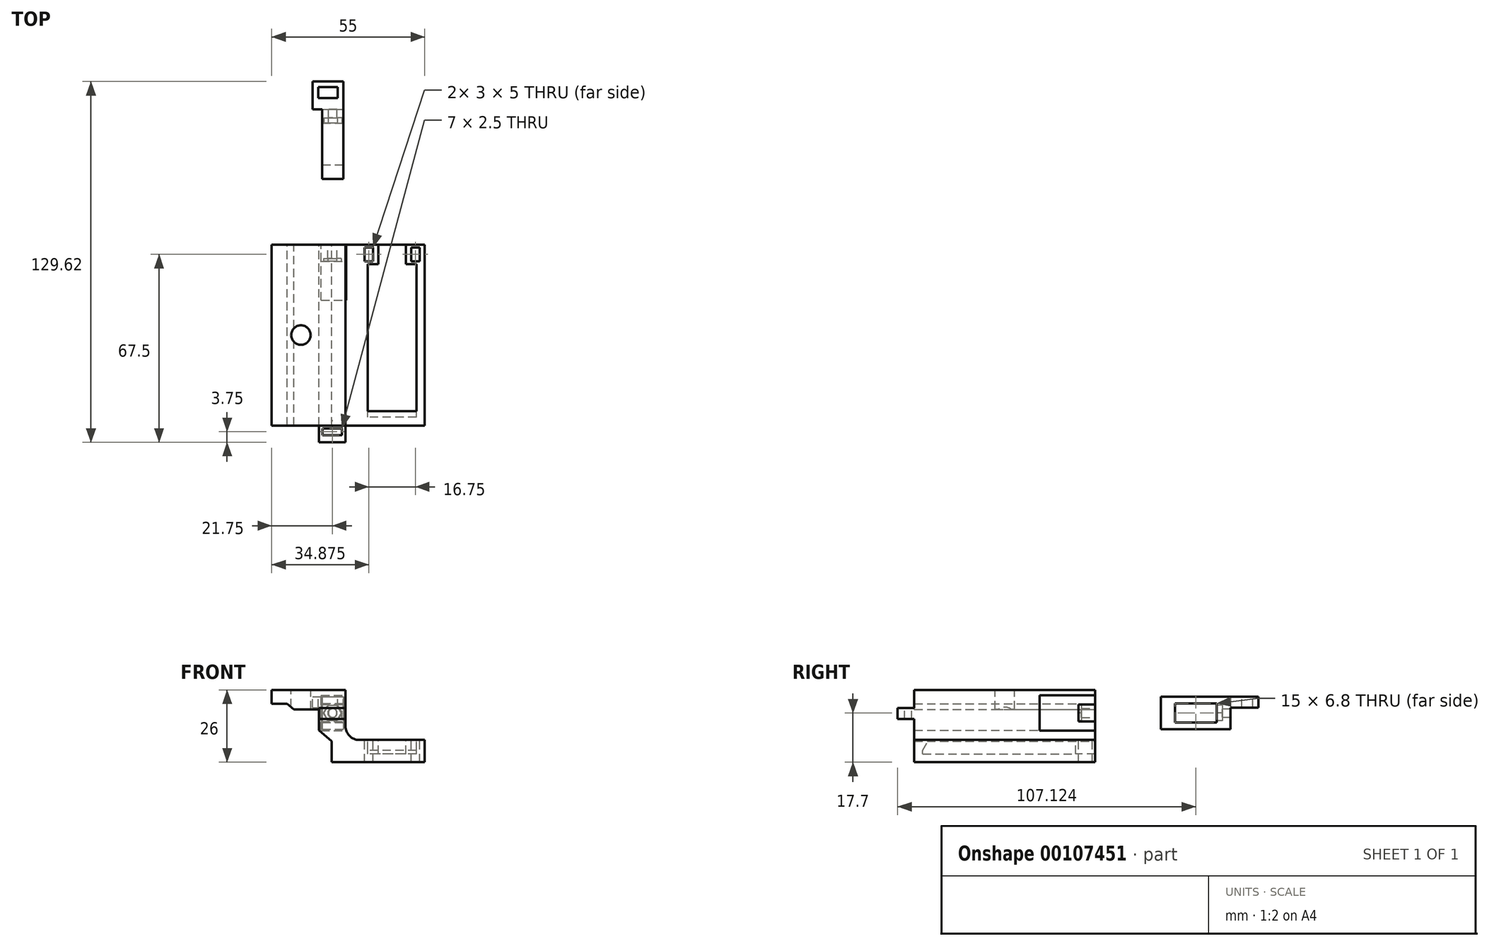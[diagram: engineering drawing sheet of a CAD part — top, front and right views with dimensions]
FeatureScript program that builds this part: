
annotation { "Feature Type Name" : "Feature", "Feature Type Description" : "" }
export const myFeature = defineFeature(function(context is Context, id is Id, definition is map)
    precondition{}
    {
        {
            var Q0;
            Q0=qCreatedBy(makeId("Front.planeOp"),FACE);
            var sketch = newSketch(context, id + "F0", { "sketchPlane" : qUnion([Q0])});
            skLineSegment(sketch, "E0", {"start": v(0, 0) * mm, "end": v(0, 21) * mm, "construction": true});
            skLineSegment(sketch, "E1", {"start": v(0, 0) * mm, "end": v(21.5, 0) * mm, "construction": true});
            skLineSegment(sketch, "E2", {"start": v(0, 21) * mm, "end": v(5.5, 21) * mm});
            skLineSegment(sketch, "E3", {"start": v(8, 19) * mm, "end": v(17, 19) * mm});
            skLineSegment(sketch, "E4", {"start": v(17, 19) * mm, "end": v(17, 11.5) * mm});
            skLineSegment(sketch, "E5", {"start": v(21.5, 0) * mm, "end": v(21.5, 7.5) * mm});
            skLineSegment(sketch, "E6", {"start": v(17, 11.5) * mm, "end": v(21.5, 7.5) * mm});
            skLineSegment(sketch, "E7", {"start": v(5.5, 21) * mm, "end": v(8, 19) * mm});
            skLineSegment(sketch, "E8", {"start": v(0, 21) * mm, "end": v(0, 26) * mm});
            skLineSegment(sketch, "E9", {"start": v(26.5, 13) * mm, "end": v(26.5, 26) * mm});
            skLineSegment(sketch, "E10", {"start": v(0, 26) * mm, "end": v(26.5, 26) * mm});
            skLineSegment(sketch, "E11", {"start": v(21.5, 0) * mm, "end": v(55, 0) * mm});
            skLineSegment(sketch, "E12", {"start": v(55, 0) * mm, "end": v(55, 8) * mm});
            skLineSegment(sketch, "E13", {"start": v(55, 8) * mm, "end": v(31.5, 8) * mm});
            skPoint(sketch, "E14.visualSharp", {"position": v(26.5, 26) * mm});
            skPoint(sketch, "E15.visualSharp", {"position": v(26.5, 8) * mm});
            skArc(sketch, "E15.filletArc", {"start": v(26.5, 13) * mm, "mid": v(27.96, 9.46) * mm, "end": v(31.5, 8) * mm});
            skSolve(sketch);
        }
        {
            var Q0;
            Q0=makeQuery(id+"F0.imprint","IMPRINT",FACE,{"disambiguationData":[TD([[makeQuery(id+"F0.imprint","IMPRINT",EDGE,{"derivedFrom":sQuery(id+"F0.wireOp",EDGE,"E2")}),1.0]])]});
            extrude(context, id + "F1", {"entities" : qUnion([Q0]), "depth" : 65 * mm});
        }
        {
            var Q0;
            Q0=makeQuery(id+"F1.opExtrude","SWEPT_FACE",FACE,{"disambiguationData":[OSD([sQuery(id+"F0.wireOp",EDGE,"E10")])]});
            var sketch = newSketch(context, id + "F2", { "sketchPlane" : qUnion([Q0])});
            skLineSegment(sketch, "E16", {"start": v(10.5, 0) * mm, "end": v(10.5, -65) * mm, "construction": true});
            skCircle(sketch, "E17", {"center": v(10.5, -32.5) * mm, "radius": 3.5 * mm});
            skSolve(sketch);
        }
        {
            var Q0;
            Q0=makeQuery(id+"F2.imprint","IMPRINT",FACE,{"disambiguationData":[TD([[makeQuery(id+"F2.imprint","IMPRINT",EDGE,{"derivedFrom":sQuery(id+"F2.wireOp",EDGE,"E17")}),1.0]])]});
            extrude(context, id + "F3", {"entities" : qUnion([Q0]), "operationType" : NewBodyOperationType.REMOVE, "endBound" : BoundingType.UP_TO_NEXT, "oppositeDirection" : true, "depth" : 25 * mm});
        }
        {
            var Q0;
            Q0=makeQuery(id+"F1.opExtrude","SWEPT_FACE",FACE,{"disambiguationData":[OSD([sQuery(id+"F0.wireOp",EDGE,"E13")])]});
            var sketch = newSketch(context, id + "F4", { "sketchPlane" : qUnion([Q0])});
            skLineSegment(sketch, "E18.bottom", {"start": v(52, -62) * mm, "end": v(34.5, -62) * mm});
            skLineSegment(sketch, "E18.top", {"start": v(52, -7) * mm, "end": v(48.25, -7) * mm});
            skLineSegment(sketch, "E18.left", {"start": v(52, -62) * mm, "end": v(52, -7) * mm});
            skLineSegment(sketch, "E18.right", {"start": v(34.5, -62) * mm, "end": v(34.5, -7) * mm});
            skLineSegment(sketch, "E19", {"start": v(38.25, -7) * mm, "end": v(38.25, 0) * mm});
            skLineSegment(sketch, "E20", {"start": v(38.25, 0) * mm, "end": v(48.25, 0) * mm});
            skLineSegment(sketch, "E21", {"start": v(48.25, 0) * mm, "end": v(48.25, -7) * mm});
            skLineSegment(sketch, "E22.trimOffspring", {"start": v(38.25, -7) * mm, "end": v(34.5, -7) * mm});
            skLineSegment(sketch, "E23", {"start": v(43.25, -62) * mm, "end": v(43.25, -65) * mm, "construction": true});
            skSolve(sketch);
        }
        {
            var Q0;
            Q0=makeQuery(id+"F4.imprint","IMPRINT",FACE,{"disambiguationData":[TD([[makeQuery(id+"F4.imprint","IMPRINT",EDGE,{"derivedFrom":sQuery(id+"F4.wireOp",EDGE,"E18.bottom")}),-1.0]])]});
            extrude(context, id + "F5", {"entities" : qUnion([Q0]), "operationType" : NewBodyOperationType.REMOVE, "oppositeDirection" : true, "depth" : 5 * mm});
        }
        {
            var Q0;
            Q0=makeQuery(id+"F5.boolean.opBoolean","COPY",FACE,{"derivedFrom":makeQuery(id+"F5.opExtrude","SWEPT_FACE",FACE,{"disambiguationData":[OSD([sQuery(id+"F4.wireOp",EDGE,"E18.right")])]})});
            var sketch = newSketch(context, id + "F6", { "sketchPlane" : qUnion([Q0])});
            skLineSegment(sketch, "E24", {"start": v(-62, 4.3) * mm, "end": v(-59.86, 8) * mm});
            skSolve(sketch);
        }
        {
            var Q0;
            {var subQ0=sQuery(id+"F6.wireOp",EDGE,"E24");Q0=makeQuery(id+"F6.imprint","IMPRINT",FACE,{"disambiguationData":[TD([[makeQuery(id+"F6.imprint","IMPRINT",EDGE,{"derivedFrom":subQ0}),1.0]])]});}
            extrude(context, id + "F7", {"entities" : qUnion([Q0]), "operationType" : NewBodyOperationType.ADD, "endBound" : BoundingType.UP_TO_NEXT, "depth" : 25 * mm});
        }
        {
            var Q0;
            Q0=makeQuery(id+"F1.opExtrude","SWEPT_FACE",FACE,{"disambiguationData":[OSD([sQuery(id+"F0.wireOp",EDGE,"E9")])]});
            cPlane(context, id + "F8", {"entities" : qUnion([Q0]), "cplaneType" : CPlaneType.OFFSET, "offset" : 0 * mm, "oppositeDirection" : true, "width" : 150 * mm, "height" : 150 * mm});
        }
        {
            var Q0;
            Q0=qCreatedBy(id+"F8.planeOp",FACE);
            var sketch = newSketch(context, id + "F9", { "sketchPlane" : qUnion([Q0])});
            skLineSegment(sketch, "E25.bottom", {"start": v(-58, 13) * mm, "end": v(0, 13) * mm});
            skLineSegment(sketch, "E25.top", {"start": v(-65, 15.5) * mm, "end": v(0, 15.5) * mm});
            skLineSegment(sketch, "E25.right", {"start": v(0, 13) * mm, "end": v(0, 15.5) * mm});
            skLineSegment(sketch, "E26.left", {"start": v(-65, 15.5) * mm, "end": v(-65, 13) * mm});
            skPoint(sketch, "E27", {"position": v(-29, 13) * mm});
            skLineSegment(sketch, "E28", {"start": v(-29, 18.78) * mm, "end": v(-29, 7.34) * mm, "construction": true});
            skLineSegment(sketch, "E29.MirrorCS", {"start": v(0, 15.5) * mm, "end": v(0, 13) * mm});
            skLineSegment(sketch, "E30.MirrorCS", {"start": v(7, 15.5) * mm, "end": v(7, 13) * mm});
            skLineSegment(sketch, "E31.bottom", {"start": v(-65, 15.5) * mm, "end": v(-71, 15.5) * mm});
            skLineSegment(sketch, "E31.top", {"start": v(-65, 19.5) * mm, "end": v(-71, 19.5) * mm});
            skLineSegment(sketch, "E31.left", {"start": v(-65, 15.5) * mm, "end": v(-65, 19.5) * mm});
            skLineSegment(sketch, "E31.right", {"start": v(-71, 15.5) * mm, "end": v(-71, 19.5) * mm});
            skLineSegment(sketch, "E32.MirrorCS", {"start": v(7, 15.5) * mm, "end": v(7, 19.5) * mm});
            skSolve(sketch);
        }
        {
            var Q0;
            Q0=makeQuery(id+"F9.imprint","IMPRINT",FACE,{"disambiguationData":[TD([[makeQuery(id+"F9.imprint","IMPRINT",EDGE,{"derivedFrom":sQuery(id+"F9.wireOp",EDGE,"E31.bottom")}),-1.0]])]});
            var Q1;
            Q1=makeQuery(id+"F9.imprint","IMPRINT",FACE,{"disambiguationData":[TD([[makeQuery(id+"F9.imprint","IMPRINT",EDGE,{"derivedFrom":sQuery(id+"F9.wireOp",EDGE,"28a8ac16-13eb-431f-9eda-ab6bdd291a540.MirrorCS")}),-1.0]])]});
            var Q2;
            Q2=makeQuery(id+"F1.opExtrude","SWEPT_FACE",FACE,{"disambiguationData":[OSD([sQuery(id+"F0.wireOp",EDGE,"E4")])]});
            extrude(context, id + "F10", {"entities" : qUnion([Q0, Q1]), "operationType" : NewBodyOperationType.ADD, "endBound" : BoundingType.UP_TO_SURFACE, "oppositeDirection" : true, "endBoundEntityFace" : qUnion([Q2]), "depth" : 25 * mm});
        }
        {
            var Q0;
            Q0=makeQuery(id+"F10.opExtrude","SWEPT_FACE",FACE,{"disambiguationData":[OSD([sQuery(id+"F9.wireOp",EDGE,"E31.top")])]});
            var sketch = newSketch(context, id + "F11", { "sketchPlane" : qUnion([Q0])});
            skLineSegment(sketch, "E33.bottom", {"start": v(18.25, -66) * mm, "end": v(25.25, -66) * mm});
            skLineSegment(sketch, "E33.top", {"start": v(18.25, -68.5) * mm, "end": v(25.25, -68.5) * mm});
            skLineSegment(sketch, "E33.left", {"start": v(18.25, -66) * mm, "end": v(18.25, -68.5) * mm});
            skLineSegment(sketch, "E33.right", {"start": v(25.25, -66) * mm, "end": v(25.25, -68.5) * mm});
            skLineSegment(sketch, "E34", {"start": v(21.75, -71) * mm, "end": v(21.75, -68.5) * mm, "construction": true});
            skSolve(sketch);
        }
        {
            var Q0;
            Q0=makeQuery(id+"F11.imprint","IMPRINT",FACE,{"disambiguationData":[TD([[makeQuery(id+"F11.imprint","IMPRINT",EDGE,{"derivedFrom":sQuery(id+"F11.wireOp",EDGE,"E33.bottom")}),-1.0]])]});
            extrude(context, id + "F12", {"entities" : qUnion([Q0]), "operationType" : NewBodyOperationType.REMOVE, "endBound" : BoundingType.UP_TO_NEXT, "oppositeDirection" : true, "depth" : 25 * mm});
        }
        {
            var Q0;
            Q0=qCreatedBy(id+"F8.planeOp",FACE);
            cPlane(context, id + "F13", {"entities" : qUnion([Q0]), "cplaneType" : CPlaneType.OFFSET, "offset" : 0.75 * mm, "oppositeDirection" : true, "width" : 150 * mm, "height" : 150 * mm});
        }
        {
            var Q0;
            Q0=qCreatedBy(id+"F13.planeOp",FACE);
            var sketch = newSketch(context, id + "F14", { "sketchPlane" : qUnion([Q0])});
            skLineSegment(sketch, "E35", {"start": v(0, 11.4) * mm, "end": v(-20, 11.4) * mm});
            skLineSegment(sketch, "E36", {"start": v(-20, 24) * mm, "end": v(0, 24) * mm});
            skLineSegment(sketch, "E37", {"start": v(0, 24) * mm, "end": v(0, 20.7) * mm});
            skLineSegment(sketch, "E38", {"start": v(0, 20.7) * mm, "end": v(-6, 20.7) * mm});
            skLineSegment(sketch, "E39", {"start": v(-6, 20.7) * mm, "end": v(-6, 14.7) * mm});
            skLineSegment(sketch, "E40", {"start": v(-6, 14.7) * mm, "end": v(0, 14.7) * mm});
            skLineSegment(sketch, "E41", {"start": v(0, 14.7) * mm, "end": v(0, 11.4) * mm});
            skLineSegment(sketch, "E42", {"start": v(-20, 11.4) * mm, "end": v(-20, 24) * mm});
            skSolve(sketch);
        }
        {
            var Q0;
            Q0=makeQuery(id+"F14.imprint","IMPRINT",FACE,{"disambiguationData":[TD([[makeQuery(id+"F14.imprint","IMPRINT",EDGE,{"derivedFrom":sQuery(id+"F14.wireOp",EDGE,"E35")}),-1.0]])]});
            extrude(context, id + "F15", {"entities" : qUnion([Q0]), "operationType" : NewBodyOperationType.REMOVE, "oppositeDirection" : true, "depth" : 8 * mm});
        }
        {
            var Q0;
            Q0=makeQuery(id+"F1.opExtrude","CAP_FACE",FACE,{"disambiguationData":[OSD([sQuery(id+"F0.wireOp",EDGE,"E2"),sQuery(id+"F0.wireOp",EDGE,"E3"),sQuery(id+"F0.wireOp",EDGE,"E4"),sQuery(id+"F0.wireOp",EDGE,"E5"),sQuery(id+"F0.wireOp",EDGE,"E6"),sQuery(id+"F0.wireOp",EDGE,"E7"),sQuery(id+"F0.wireOp",EDGE,"E8"),sQuery(id+"F0.wireOp",EDGE,"E9"),sQuery(id+"F0.wireOp",EDGE,"E10"),sQuery(id+"F0.wireOp",EDGE,"E11"),sQuery(id+"F0.wireOp",EDGE,"E12"),sQuery(id+"F0.wireOp",EDGE,"E13"),sQuery(id+"F0.wireOp",EDGE,"E14.filletArc"),sQuery(id+"F0.wireOp",EDGE,"E15.filletArc")])],"isStart":true});
            var sketch = newSketch(context, id + "F16", { "sketchPlane" : qUnion([Q0])});
            skLineSegment(sketch, "E43", {"start": v(-25.75, 17.7) * mm, "end": v(-17.75, 17.7) * mm, "construction": true});
            skPoint(sketch, "E44", {"position": v(-21.75, 17.7) * mm});
            skCircle(sketch, "E45", {"center": v(-21.75, 17.7) * mm, "radius": 1.65 * mm});
            skPoint(sketch, "E46.0.midPoint", {"position": v(-21.05, 15.93) * mm});
            skLineSegment(sketch, "E47", {"start": v(-17.75, 20.7) * mm, "end": v(-17.75, 14.7) * mm, "construction": true});
            skSolve(sketch);
        }
        {
            var Q0;
            Q0=makeQuery(id+"F16.imprint","IMPRINT",FACE,{"disambiguationData":[TD([[makeQuery(id+"F16.imprint","IMPRINT",EDGE,{"derivedFrom":sQuery(id+"F16.wireOp",EDGE,"E45")}),1.0]])]});
            extrude(context, id + "F17", {"entities" : qUnion([Q0]), "operationType" : NewBodyOperationType.REMOVE, "endBound" : BoundingType.UP_TO_NEXT, "oppositeDirection" : true, "depth" : 25 * mm});
        }
        {
            var Q0;
            Q0=makeQuery(id+"F15.boolean.opBoolean","COPY",FACE,{"derivedFrom":makeQuery(id+"F15.opExtrude","SWEPT_FACE",FACE,{"disambiguationData":[OSD([sQuery(id+"F14.wireOp",EDGE,"E39")])]})});
            var sketch = newSketch(context, id + "F18", { "sketchPlane" : qUnion([Q0])});
            skCircle(sketch, "E48.cCircle", {"center": v(21.75, 17.7) * mm, "radius": 2.75 * mm, "construction": true});
            skLineSegment(sketch, "E48.0", {"start": v(24.93, 17.7) * mm, "end": v(23.34, 14.95) * mm});
            skLineSegment(sketch, "E48.1", {"start": v(23.34, 14.95) * mm, "end": v(20.16, 14.95) * mm});
            skLineSegment(sketch, "E48.2", {"start": v(20.16, 14.95) * mm, "end": v(18.57, 17.7) * mm});
            skLineSegment(sketch, "E48.3", {"start": v(18.57, 17.7) * mm, "end": v(20.16, 20.45) * mm});
            skLineSegment(sketch, "E48.4", {"start": v(20.16, 20.45) * mm, "end": v(23.34, 20.45) * mm});
            skLineSegment(sketch, "E48.5", {"start": v(23.34, 20.45) * mm, "end": v(24.93, 17.7) * mm});
            skPoint(sketch, "E48.0.midPoint", {"position": v(24.13, 16.33) * mm});
            skSolve(sketch);
        }
        {
            var Q0;
            {var subQ1=sQuery(id+"F18.wireOp",EDGE,"E48.1");Q0=makeQuery(id+"F18.imprint","IMPRINT",FACE,{"disambiguationData":[TD([[makeQuery(id+"F18.imprint","IMPRINT",EDGE,{"derivedFrom":subQ1}),-1.0]])]});}
            extrude(context, id + "F19", {"entities" : qUnion([Q0]), "operationType" : NewBodyOperationType.REMOVE, "oppositeDirection" : true, "depth" : 1 * mm});
        }
        {
            var Q0;
            Q0 = qSketchRegion(id + "F14", true);
            extrude(context, id + "F20", {"entities" : qUnion([Q0]), "operationType" : NewBodyOperationType.REMOVE, "endBound" : BoundingType.UP_TO_NEXT, "oppositeDirection" : true, "depth" : 25 * mm});
        }
        {
            var Q0;
            Q0 = qSketchRegion(id + "F14", true);
            extrude(context, id + "F21", {"entities" : qUnion([Q0]), "operationType" : NewBodyOperationType.REMOVE, "endBound" : BoundingType.UP_TO_NEXT, "depth" : 25 * mm});
        }
        {
            var Q0;
            Q0=makeQuery(id+"F7.boolean.opBoolean","MERGE",FACE,{"derivedFrom":[makeQuery(id+"F1.opExtrude","SWEPT_FACE",FACE,{"disambiguationData":[OSD([sQuery(id+"F0.wireOp",EDGE,"E13")])]}),makeQuery(id+"F7.opExtrude","SWEPT_FACE",FACE,{"disambiguationData":[OSD([sQuery(id+"F4.wireOp",EDGE,"E18.right")])]})]});
            var sketch = newSketch(context, id + "F22", { "sketchPlane" : qUnion([Q0])});
            skLineSegment(sketch, "E49.bottom", {"start": v(36.38, -1) * mm, "end": v(33.38, -1) * mm});
            skLineSegment(sketch, "E49.top", {"start": v(36.38, -6) * mm, "end": v(33.38, -6) * mm});
            skLineSegment(sketch, "E49.left", {"start": v(36.38, -1) * mm, "end": v(36.38, -6) * mm});
            skLineSegment(sketch, "E49.right", {"start": v(33.38, -1) * mm, "end": v(33.38, -6) * mm});
            skPoint(sketch, "E49.middle", {"position": v(34.88, -3.5) * mm});
            skLineSegment(sketch, "E50", {"start": v(48.25, -7) * mm, "end": v(38.25, -7) * mm, "construction": true});
            skLineSegment(sketch, "E51", {"start": v(43.25, -7) * mm, "end": v(43.25, 0.02) * mm, "construction": true});
            skLineSegment(sketch, "E52.MirrorCS", {"start": v(50.12, -1) * mm, "end": v(50.12, -6) * mm});
            skLineSegment(sketch, "E53.MirrorCS", {"start": v(50.12, -6) * mm, "end": v(53.12, -6) * mm});
            skLineSegment(sketch, "E54.MirrorCS", {"start": v(53.12, -1) * mm, "end": v(53.12, -6) * mm});
            skLineSegment(sketch, "E55.MirrorCS", {"start": v(50.12, -1) * mm, "end": v(53.12, -1) * mm});
            skLineSegment(sketch, "E56", {"start": v(36.38, -3.5) * mm, "end": v(38.25, -3.5) * mm, "construction": true});
            skLineSegment(sketch, "E57", {"start": v(34.88, -3.5) * mm, "end": v(34.88, 0) * mm, "construction": true});
            skSolve(sketch);
        }
        {
            var Q0;
            Q0=makeQuery(id+"F22.imprint","IMPRINT",FACE,{"disambiguationData":[TD([[makeQuery(id+"F22.imprint","IMPRINT",EDGE,{"derivedFrom":sQuery(id+"F22.wireOp",EDGE,"E49.bottom")}),1.0]])]});
            var Q1;
            Q1=makeQuery(id+"F22.imprint","IMPRINT",FACE,{"disambiguationData":[TD([[makeQuery(id+"F22.imprint","IMPRINT",EDGE,{"derivedFrom":sQuery(id+"F22.wireOp",EDGE,"E52.MirrorCS")}),1.0]])]});
            extrude(context, id + "F23", {"entities" : qUnion([Q0, Q1]), "operationType" : NewBodyOperationType.REMOVE, "endBound" : BoundingType.UP_TO_NEXT, "oppositeDirection" : true, "depth" : 25 * mm});
        }
        {
            var Q0;
            Q0=qCreatedBy(id+"F13.planeOp",FACE);
            var sketch = newSketch(context, id + "F24", { "sketchPlane" : qUnion([Q0])});
            skLineSegment(sketch, "E58.bottom", {"start": v(23.62, 23.6) * mm, "end": v(48.62, 23.6) * mm});
            skLineSegment(sketch, "E58.top", {"start": v(23.62, 11.8) * mm, "end": v(48.62, 11.8) * mm});
            skLineSegment(sketch, "E59", {"start": v(43.62, 14.3) * mm, "end": v(28.62, 14.3) * mm});
            skLineSegment(sketch, "E60", {"start": v(28.62, 14.3) * mm, "end": v(28.62, 21.1) * mm});
            skLineSegment(sketch, "E61", {"start": v(28.62, 21.1) * mm, "end": v(43.62, 21.1) * mm});
            skLineSegment(sketch, "E62", {"start": v(43.62, 21.1) * mm, "end": v(43.62, 14.3) * mm});
            skLineSegment(sketch, "E63", {"start": v(48.62, 23.6) * mm, "end": v(48.62, 11.8) * mm});
            skLineSegment(sketch, "E64", {"start": v(23.62, 23.6) * mm, "end": v(23.62, 11.8) * mm});
            skLineSegment(sketch, "E65", {"start": v(23.62, 17.7) * mm, "end": v(28.62, 17.7) * mm, "construction": true});
            skLineSegment(sketch, "E66", {"start": v(28.62, 17.7) * mm, "end": v(43.62, 17.7) * mm, "construction": true});
            skLineSegment(sketch, "E67", {"start": v(43.62, 17.7) * mm, "end": v(48.62, 17.7) * mm, "construction": true});
            skSolve(sketch);
        }
        {
            var Q0;
            Q0=makeQuery(id+"F24.imprint","IMPRINT",FACE,{"disambiguationData":[TD([[makeQuery(id+"F24.imprint","IMPRINT",EDGE,{"derivedFrom":sQuery(id+"F24.wireOp",EDGE,"E58.bottom")}),-1.0]])]});
            extrude(context, id + "F25", {"entities" : qUnion([Q0]), "oppositeDirection" : true, "depth" : 7.6 * mm});
        }
        {
            var Q0;
            Q0=makeQuery(id+"F25.opExtrude","SWEPT_FACE",FACE,{"disambiguationData":[OSD([sQuery(id+"F24.wireOp",EDGE,"E63")])]});
            var sketch = newSketch(context, id + "F26", { "sketchPlane" : qUnion([Q0])});
            skLineSegment(sketch, "E68", {"start": v(-25.75, 17.7) * mm, "end": v(-18.15, 17.7) * mm, "construction": true});
            skCircle(sketch, "E69", {"center": v(-21.95, 17.7) * mm, "radius": 1.55 * mm});
            skSolve(sketch);
        }
        {
            var Q0;
            Q0=makeQuery(id+"F26.imprint","IMPRINT",FACE,{"disambiguationData":[TD([[makeQuery(id+"F26.imprint","IMPRINT",EDGE,{"derivedFrom":sQuery(id+"F26.wireOp",EDGE,"E69")}),1.0]])]});
            var Q1;
            Q1=sQuery(id+"F26.wireOp",EDGE,"E69");
            extrude(context, id + "F27", {"entities" : qUnion([Q0]), "operationType" : NewBodyOperationType.REMOVE, "surfaceEntities" : qUnion([Q1]), "endBound" : BoundingType.UP_TO_NEXT, "oppositeDirection" : true, "depth" : 25 * mm});
        }
        {
            var Q0;
            Q0=makeQuery(id+"F25.opExtrude","SWEPT_FACE",FACE,{"disambiguationData":[OSD([sQuery(id+"F24.wireOp",EDGE,"E62")])]});
            var sketch = newSketch(context, id + "F28", { "sketchPlane" : qUnion([Q0])});
            skCircle(sketch, "E70.cCircle", {"center": v(21.95, 17.7) * mm, "radius": 2.8 * mm, "construction": true});
            skLineSegment(sketch, "E70.0", {"start": v(25.18, 17.7) * mm, "end": v(23.57, 14.9) * mm});
            skLineSegment(sketch, "E70.1", {"start": v(23.57, 14.9) * mm, "end": v(20.33, 14.9) * mm});
            skLineSegment(sketch, "E70.2", {"start": v(20.33, 14.9) * mm, "end": v(18.72, 17.7) * mm});
            skLineSegment(sketch, "E70.3", {"start": v(18.72, 17.7) * mm, "end": v(20.33, 20.5) * mm});
            skLineSegment(sketch, "E70.4", {"start": v(20.33, 20.5) * mm, "end": v(23.57, 20.5) * mm});
            skLineSegment(sketch, "E70.5", {"start": v(23.57, 20.5) * mm, "end": v(25.18, 17.7) * mm});
            skPoint(sketch, "E70.0.midPoint", {"position": v(24.37, 16.3) * mm});
            skSolve(sketch);
        }
        {
            var Q0;
            Q0=makeQuery(id+"F28.imprint","IMPRINT",FACE,{"disambiguationData":[TD([[makeQuery(id+"F28.imprint","IMPRINT",EDGE,{"derivedFrom":sQuery(id+"F28.wireOp",EDGE,"E70.0")}),-1.0]])]});
            extrude(context, id + "F29", {"entities" : qUnion([Q0]), "operationType" : NewBodyOperationType.REMOVE, "oppositeDirection" : true, "depth" : 2 * mm});
        }
        {
            var Q0;
            Q0=makeQuery(id+"F25.opExtrude","SWEPT_FACE",FACE,{"disambiguationData":[OSD([sQuery(id+"F24.wireOp",EDGE,"E58.bottom")])]});
            var sketch = newSketch(context, id + "F30", { "sketchPlane" : qUnion([Q0])});
            skLineSegment(sketch, "E71.bottom", {"start": v(14.75, 48.62) * mm, "end": v(25.75, 48.62) * mm});
            skLineSegment(sketch, "E71.top", {"start": v(14.75, 58.62) * mm, "end": v(25.75, 58.62) * mm});
            skLineSegment(sketch, "E71.left", {"start": v(14.75, 48.62) * mm, "end": v(14.75, 58.62) * mm});
            skLineSegment(sketch, "E71.right", {"start": v(25.75, 48.62) * mm, "end": v(25.75, 58.62) * mm});
            skLineSegment(sketch, "E72.0", {"start": v(16.75, 52.62) * mm, "end": v(23.75, 52.62) * mm});
            skLineSegment(sketch, "E73.0", {"start": v(16.75, 56.62) * mm, "end": v(23.75, 56.62) * mm});
            skLineSegment(sketch, "E74.0", {"start": v(16.75, 52.62) * mm, "end": v(16.75, 56.62) * mm});
            skLineSegment(sketch, "E75.0", {"start": v(23.75, 52.62) * mm, "end": v(23.75, 56.62) * mm});
            skLineSegment(sketch, "E76", {"start": v(25.75, 52.32) * mm, "end": v(23.75, 52.32) * mm, "construction": true});
            skLineSegment(sketch, "E77", {"start": v(22, 58.62) * mm, "end": v(22, 56.62) * mm, "construction": true});
            skLineSegment(sketch, "E78", {"start": v(14.75, 51.21) * mm, "end": v(16.75, 51.21) * mm, "construction": true});
            skSolve(sketch);
        }
        {
            var Q0;
            Q0=makeQuery(id+"F30.imprint","IMPRINT",FACE,{"disambiguationData":[TD([[makeQuery(id+"F30.imprint","IMPRINT",EDGE,{"derivedFrom":sQuery(id+"F30.wireOp",EDGE,"E71.bottom")}),1.0]])]});
            extrude(context, id + "F31", {"entities" : qUnion([Q0]), "operationType" : NewBodyOperationType.ADD, "oppositeDirection" : true, "depth" : 4 * mm});
        }
    });
